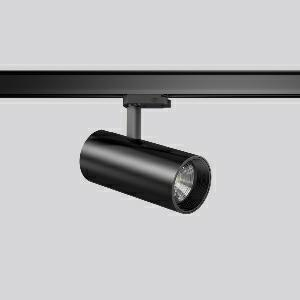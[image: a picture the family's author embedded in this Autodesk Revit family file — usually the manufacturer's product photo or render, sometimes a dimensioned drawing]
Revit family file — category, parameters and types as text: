
# Revit family: deecos_s_mini_742199_003_76_b18c
name_source: partatom
category: Lighting Fixtures
units: mm (PartAtom-declared; Revit-internal decimal feet)

## family parameters
Cut with Voids When Loaded = No
Host = Face
Light Source = No
Part Type = Normal
Room Calculation Point = No
Round Connector Dimension = Use Diameter
Shared = No

## types (1)
- DEECOS S mini (1 x LED Modul 930, 2100 lm, 3000)
    Apparent Load = 20 VA
    Approval mark = CE
    CIE Flux Codes = 96 100 100 100 100
    Color Rendering = 90
    Color Temperature = 3000
    Default Elevation = 1800 mm
    Description = Series: DEECOS S mini
LED surface-mounted projector in modern design with no visible cooling ribs. Housing: die-cast aluminium, powder-coated. Rotation range: 356°. Swivel range: 90°. Black plastic ring and recessed LED to prevent glare from the side. Optical assembly with lens made of plastic (polycarbonate) for the best homogeneous light distribution - can be changed without tools. Best colour rendering index Ra>90. With adapter for RZB 3-circuit DALI tracks. Suitable for Track on ceiling, Wall track. High quality converter without flickering and stroboscopic effect. The following accessories can be mounted without use of tools: interchangeable lenses, decorative glasses, honeycomb louvre, clear and frosted diffusers, white interchangeable plastic ring. 
Colour: deep black, matt (RAL 9005)
Diameter: 87 mm
Height: 214 mm
Lamp: LED
Socket: without socket
Colour temperature: 3000K
Colour rendering index (CRI): 92
System power: 20 W
Rated luminous flux: 2100 lm
Luminous efficiency: 105 lm/W
Control gear: Converter, dimmable, DALI
Protection class: I
Type of protection: IP 20
    Height = 214 mm
    Lamp = 1 x LED Modul 930
    Lamp Light Flux = 2100 lm
    Lamp count = 1
    Length = 87 mm
    Lifetime = 50000 h
    Luminous efficacy = 105 lm/W
    Manufacturer = RZB
    ModVariant = No
    Model = 742199.003.76
    Mounting Place = Ceiling
    Mounting Type = Rail mounted
    Number of Poles = 1
    OnlyDefault = Yes
    Power Factor = 1
    Product Name = DEECOS S mini
    Product group = Track mounted projectors
    ProductGroupID = 301
    Protection Class = Protection class I
    Protection Degree = IP 20
    RLX_Detail_Level = 1
    RLX_Emergency_Light_Flux = 0 lm
    RLX_Emergency_Type = 0
    RLX_Emergency_Type_DB = No
    RlxData = <blob elided: 39173 chars, md5=eaf42065>
    Socket = socket
    Standby Power = 0 W
    System Light Flux = 2100 lm
    System Power = 20 W
    Type Comments = Product without accessories
    Type Image = 741930.003.jpg
    URL = http://relux.com
    VarID = ---
    Voltage = 230 V
    Voltage Range = 220-240 V
    Weight = 0.00 kg
    Width = 0 mm  [stored 0 ft]

note: [stored X ft] marks values corroborated as IEEE doubles in the binary element streams (Revit-internal decimal feet)

## geometry (parser evidence)
native form markers: Blend x4, Sweep x11
no freeform markers — native parametric forms only
